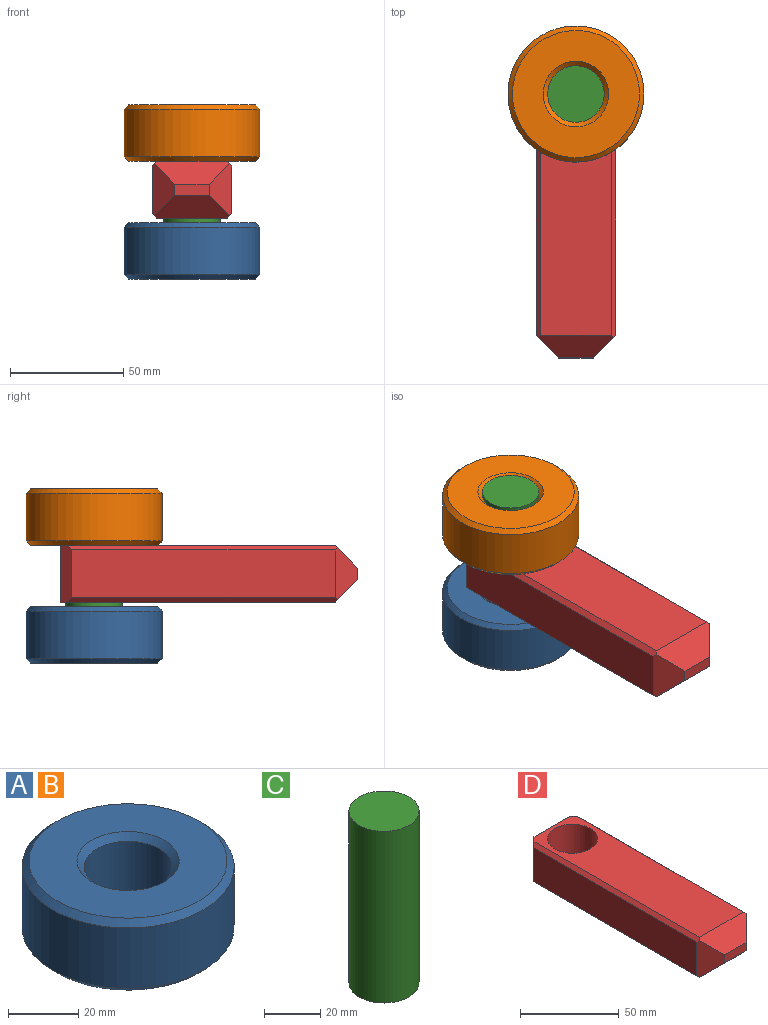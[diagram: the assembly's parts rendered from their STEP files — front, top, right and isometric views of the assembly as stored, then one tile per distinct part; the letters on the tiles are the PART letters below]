
ASSEMBLY  parts=4 mates=2
PART A: 8 faces, bbox 60.2x60.2x25 mm
  f0: cylinder r=30.1mm len=60.19mm, axis (0,0,-1), area 3971mm2, adj f4,f6
  f1: plane 56.19x56.19mm, normal (0,0,1), area 1819.3mm2, adj f4,f5
  f2: plane 56.19x56.19mm, normal (0,0,-1), area 1819.3mm2, adj f6,f7
  f3: cylinder r=12.5mm len=25mm, axis (0,0,-1), area 1649.3mm2, adj f5,f7
  f4: cone r=28.1mm half-angle=45deg, axis (0,0,-1), area 517.1mm2, adj f0,f1
  f5: cone r=12.5mm half-angle=45deg, axis (0,0,1), area 239.9mm2, adj f1,f3
  f6: cone r=30.1mm half-angle=45deg, axis (0,0,1), area 517.1mm2, adj f0,f2
  f7: cone r=14.5mm half-angle=45deg, axis (0,0,-1), area 239.9mm2, adj f2,f3
PART B: same geometry as A
PART C: 3 faces, bbox 25x25x75 mm
  f0: cylinder r=12.5mm len=75mm, axis (0,0,-1), area 5890.5mm2, adj f1,f2
  f1: plane 25x25mm, normal (0,0,1), area 490.9mm2, adj f0
  f2: plane 25x25mm, normal (0,0,-1), area 490.9mm2, adj f0
PART D: 17 faces, bbox 35.3x131.6x25 mm
  f0: plane 116.63x21mm, normal (1,0,0), area 2449.2mm2, adj f7,f10,f12,f13
  f1: plane 25.27x25mm, normal (0,1,0), area 631.8mm2, adj f3,f4,f7,f8
  f2: plane 116.63x21mm, normal (-1,0,0), area 2449.2mm2, adj f8,f9,f11,f16
  f3: plane 121.63x31.27mm, normal (0,0,1), area 3284.3mm2, adj f1,f5,f7,f8,f11,f12,f14
  f4: plane 121.63x31.27mm, normal (0,0,-1), area 3284.3mm2, adj f1,f5,f7,f8,f9,f10,f15
  f5: cylinder r=12.74mm len=25.49mm, axis (0,0,-1), area 2001.9mm2, adj f3,f4
  f6: plane 15.27x5mm, normal (0,-1,0), area 76.4mm2, adj f13,f14,f15,f16
  f7: plane 25x5mm, normal (0.71,0.71,0), area 171.1mm2, adj f0,f1,f3,f4,f10,f12
  f8: plane 25x5mm, normal (-0.71,0.71,0), area 171.1mm2, adj f1,f2,f3,f4,f9,f11
  f9: plane 119.63x2mm, normal (-0.71,0,-0.71), area 334.1mm2, adj f2,f4,f8,f15,f16
  f10: plane 119.63x2mm, normal (0.71,0,-0.71), area 334.1mm2, adj f0,f4,f7,f13,f15
  f11: plane 119.63x2mm, normal (-0.71,0,0.71), area 334.1mm2, adj f2,f3,f8,f14,f16
  f12: plane 119.63x2mm, normal (0.71,0,0.71), area 334.1mm2, adj f0,f3,f7,f13,f14
  f13: plane 23x10mm, normal (0.71,-0.71,0), area 209.3mm2, adj f0,f6,f10,f12,f14,f15
  f14: plane 33.27x10mm, normal (0,-0.71,0.71), area 354.6mm2, adj f3,f6,f11,f12,f13,f16
  f15: plane 33.27x10mm, normal (0,-0.71,-0.71), area 354.6mm2, adj f4,f6,f9,f10,f13,f16
  f16: plane 23x10mm, normal (-0.71,-0.71,0), area 209.3mm2, adj f2,f6,f9,f11,f14,f15
PLACE A t=(-10.04,35.89,-9.07)mm
PLACE B t=(-10.04,35.89,42.93)mm
PLACE C t=(-10.04,35.89,-7.07)mm
PLACE D t=(-10.04,10.05,17.93)mm
MATE revolute D.f5 <-> C.f0  axis (0,0,-1) through (-10.04,35.89,30.43)mm
MATE revolute A.f0 <-> C.f0  axis (0,0,-1) through (-10.04,35.89,-7.07)mm
